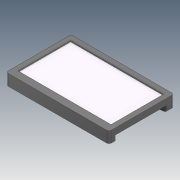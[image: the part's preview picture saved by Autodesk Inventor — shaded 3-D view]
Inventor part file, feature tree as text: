
AUTODESK INVENTOR PART (.ipt)
format: ipt  version: 2020 (Build 240168000, 168)  size: 138,752 bytes
history: mixed  units: in
note: dims shown in document units (in); Inventor stores cm internally (conversion verified against a paired STEP export)
features: other x1, chamfer x1, imported_body x1
ambient origin geometry x8: Origin, YZ Plane, XZ Plane, XY Plane, X Axis, Y Axis, Z Axis, Center Point
bodies: Body1 (imported_parasolid)
feature tree (3):
  other  "ソリッド1"
  chamfer  "Chamfer2"  [1 undecoded]
  imported_body  NMx_Import_Brep_tag  [imported B-rep: ~58 faces, bbox_mm=[267.0, 31.0, 168.4]]
note: 1 required parameter value undecoded (feature->parameter linkage not recoverable at this tier; creation-order binding heuristic only, values carry confidence <= 0.55)
